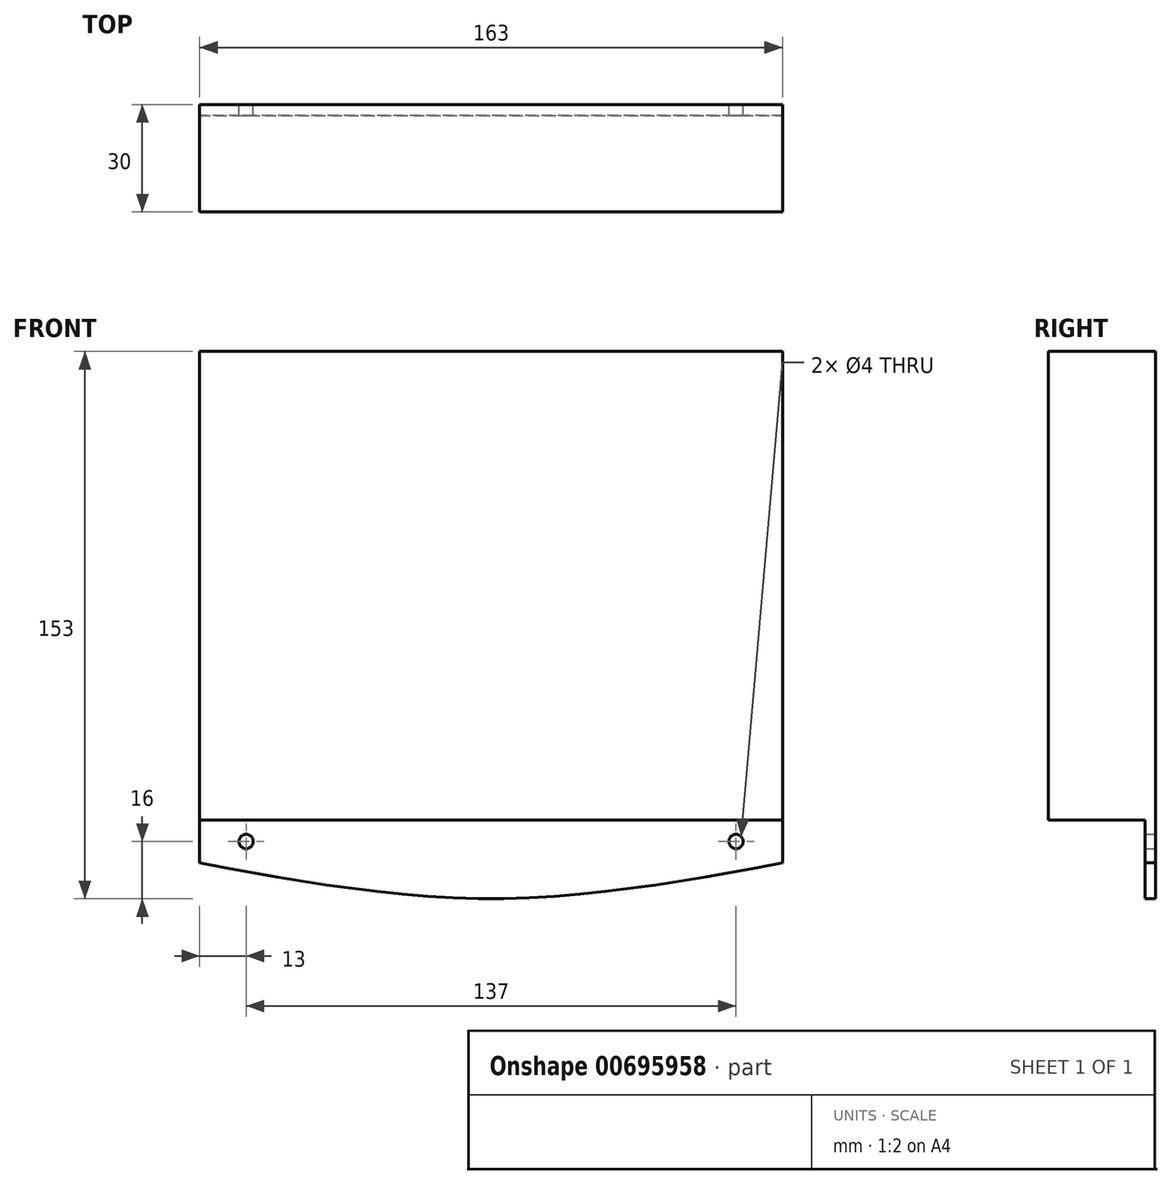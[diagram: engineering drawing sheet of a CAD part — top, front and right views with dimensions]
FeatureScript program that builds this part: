
annotation { "Feature Type Name" : "Feature", "Feature Type Description" : "" }
export const myFeature = defineFeature(function(context is Context, id is Id, definition is map)
    precondition{}
    {
        {
            var Q0;
            Q0=qCreatedBy(makeId("Front.planeOp"),FACE);
            var sketch = newSketch(context, id + "F0", { "sketchPlane" : qUnion([Q0])});
            skLineSegment(sketch, "E0.bottom", {"start": v(81.5, 65.5) * mm, "end": v(-81.5, 65.5) * mm});
            skLineSegment(sketch, "E0.top", {"start": v(81.5, -65.5) * mm, "end": v(-81.5, -65.5) * mm});
            skLineSegment(sketch, "E0.left", {"start": v(81.5, 65.5) * mm, "end": v(81.5, -65.5) * mm});
            skLineSegment(sketch, "E0.right", {"start": v(-81.5, 65.5) * mm, "end": v(-81.5, -65.5) * mm});
            skPoint(sketch, "E0.middle", {"position": v(0, 0) * mm});
            skLineSegment(sketch, "E1", {"start": v(-81.5, -65.5) * mm, "end": v(-81.5, -77.5) * mm});
            skPoint(sketch, "E2", {"position": v(0, -87.5) * mm});
            skLineSegment(sketch, "E3.MirrorCS", {"start": v(81.5, -65.5) * mm, "end": v(81.5, -77.5) * mm});
            skFitSpline(sketch, "E4", {"points": [v(-81.5, -77.5) * mm, v(0, -87.5) * mm, v(81.5, -77.5) * mm], "startDerivative": vector(163, -30) * mm, "endDerivative": vector(163, 30) * mm});
            skPoint(sketch, "E5", {"position": v(-68.5, -71.5) * mm});
            skCircle(sketch, "E6", {"center": v(-68.5, -71.5) * mm, "radius": 2 * mm});
            skCircle(sketch, "E7.MirrorC", {"center": v(68.5, -71.5) * mm, "radius": 2 * mm});
            skSolve(sketch);
        }
        {
            var Q0;
            Q0=makeQuery(id+"F0.imprint","IMPRINT",FACE,{"disambiguationData":[TD([[makeQuery(id+"F0.imprint","IMPRINT",EDGE,{"derivedFrom":sQuery(id+"F0.wireOp",EDGE,"E0.bottom")}),1.0]])]});
            extrude(context, id + "F1", {"entities" : qUnion([Q0]), "depth" : 30 * mm, "offsetDistance" : 25 * mm});
        }
        {
            var Q0;
            Q0=makeQuery(id+"F0.imprint","IMPRINT",FACE,{"disambiguationData":[TD([[makeQuery(id+"F0.imprint","IMPRINT",EDGE,{"derivedFrom":sQuery(id+"F0.wireOp",EDGE,"E0.top")}),1.0]])]});
            extrude(context, id + "F2", {"entities" : qUnion([Q0]), "operationType" : NewBodyOperationType.ADD, "depth" : 3 * mm, "offsetDistance" : 25 * mm});
        }
    });
